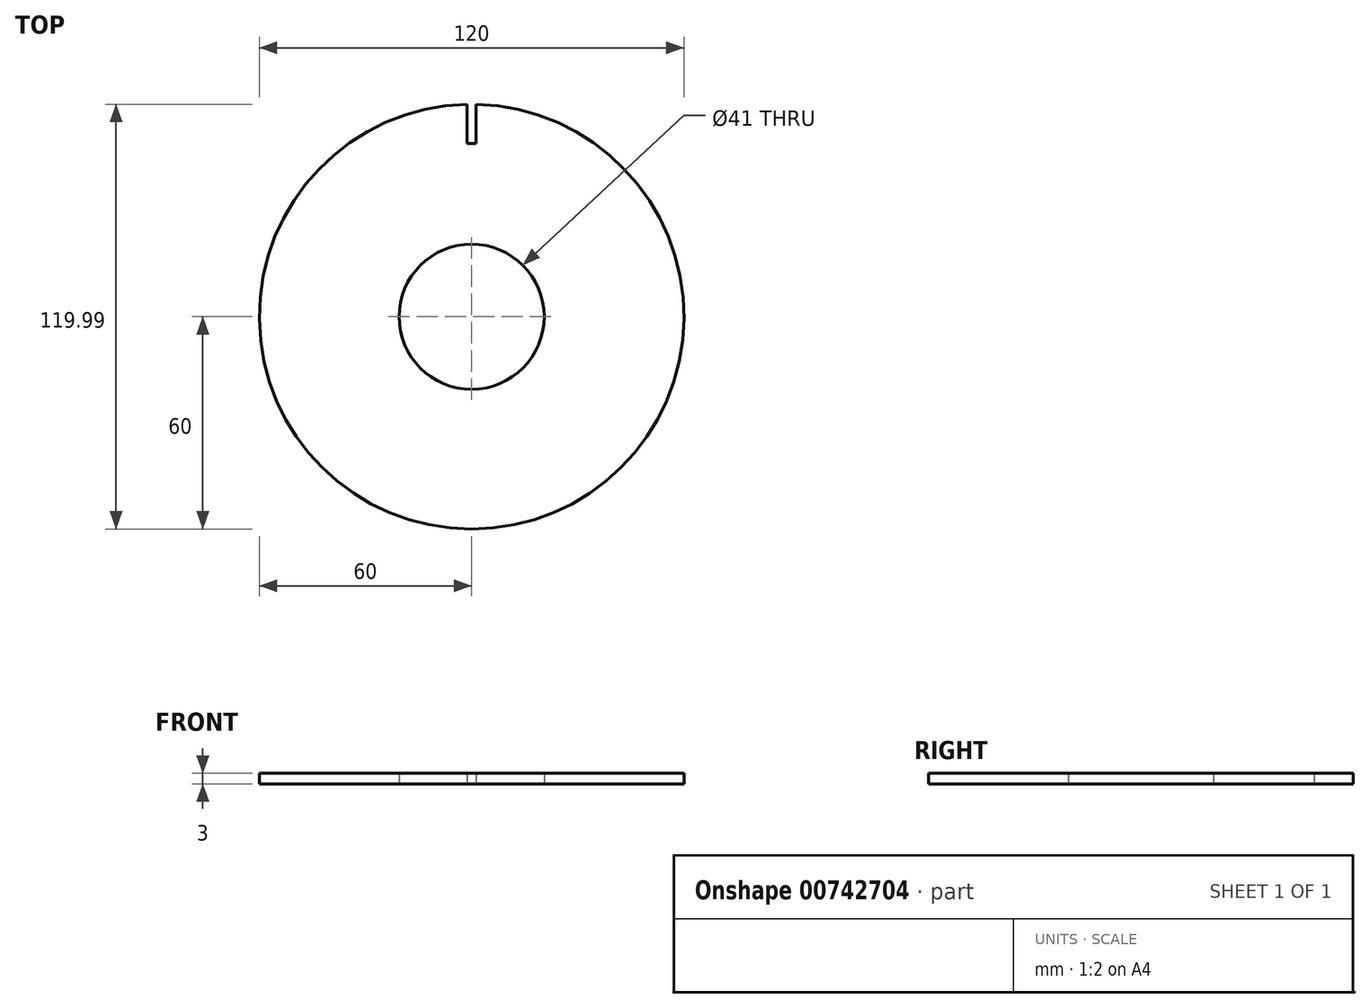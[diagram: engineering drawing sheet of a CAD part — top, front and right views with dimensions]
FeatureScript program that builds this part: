
annotation { "Feature Type Name" : "Feature", "Feature Type Description" : "" }
export const myFeature = defineFeature(function(context is Context, id is Id, definition is map)
    precondition{}
    {
        {
            var Q0;
            Q0=qCreatedBy(makeId("Top.planeOp"),FACE);
            var sketch = newSketch(context, id + "F0", { "sketchPlane" : qUnion([Q0])});
            skCircle(sketch, "E0", {"center": v(0, 0) * mm, "radius": 20.5 * mm});
            skCircle(sketch, "E1", {"center": v(0, 0) * mm, "radius": 60 * mm});
            skSolve(sketch);
        }
        {
            var Q0;
            Q0 = qSketchRegion(id + "F0", true);
            extrude(context, id + "F1", {"entities" : qUnion([Q0]), "depth" : 3 * mm, "offsetDistance" : 25 * mm});
        }
        {
            var Q0;
            Q0=qCreatedBy(makeId("Top.planeOp"),FACE);
            var sketch = newSketch(context, id + "F2", { "sketchPlane" : qUnion([Q0])});
            skLineSegment(sketch, "E2.bottom", {"start": v(-1.25, 49) * mm, "end": v(1.25, 49) * mm});
            skLineSegment(sketch, "E2.top", {"start": v(-1.25, 60) * mm, "end": v(1.25, 60) * mm});
            skLineSegment(sketch, "E2.left", {"start": v(-1.25, 49) * mm, "end": v(-1.25, 60) * mm});
            skLineSegment(sketch, "E2.right", {"start": v(1.25, 49) * mm, "end": v(1.25, 60) * mm});
            skPoint(sketch, "E2.middle", {"position": v(0, 54.5) * mm});
            skSolve(sketch);
        }
        {
            var Q0;
            Q0 = qSketchRegion(id + "F2", true);
            extrude(context, id + "F3", {"entities" : qUnion([Q0]), "operationType" : NewBodyOperationType.REMOVE, "depth" : 25 * mm, "offsetDistance" : 25 * mm});
        }
    });
